# Revit family: SpecEquip_TMV_Zip_Horne TMV & ILTDU box with bypass pipes one end
name_source: partatom
category: Specialty Equipment
revit_build: Autodesk Revit 2016 (Build: 20150220_1215(x64)
units: mm (PartAtom-declared; Revit-internal decimal feet)

## family parameters
Always vertical = Yes
Cut with Voids When Loaded = Yes
OmniClass Number = 23.65.55.14.24
OmniClass Title = Mixing Valves for Liquid Services
Part Type = Normal
Room Calculation Point = No
Round Connector Dimension = Use Diameter
Shared = No
Work Plane-Based = No

## types (1)
- ILTDU & TMV Hinged Door
    Description = Horne ILTDU & TMV: In-line Thermal Disinfection valve and Horne TMV Model H1502 in a recessed pre-plumbed box configuration with lockable Hinged stainless steel door and cold water bypass - pipes at one end
    Manufacturer = Zip Australia
    Manufacturer_Overall Depth = 74 mm  [stored 0.242782 ft]
    Manufacturer_Overall Height = 536 mm
    Manufacturer_Overall Width = 386 mm  [stored 1.2664 ft]
    Manufacturer_Spec Code = 42556
    Material_ANZRS = z_ZipTmv_Brass
    Model = Horne ILTDU - Inline Thermal Disinfection Unit & TMV H1502 in box Configuration - Hinged Door
    ModifiedIssue_ANZRS = 20171130 $
    Pipe Material = z_ZipTmv_Chrome
    Type Comments = Hinged Door
    URL = https://www.zipwater.com

note: [stored X ft] marks values corroborated as IEEE doubles in the binary element streams (Revit-internal decimal feet)

## geometry (parser evidence)
native form markers: Sweep x8
no freeform markers — native parametric forms only
